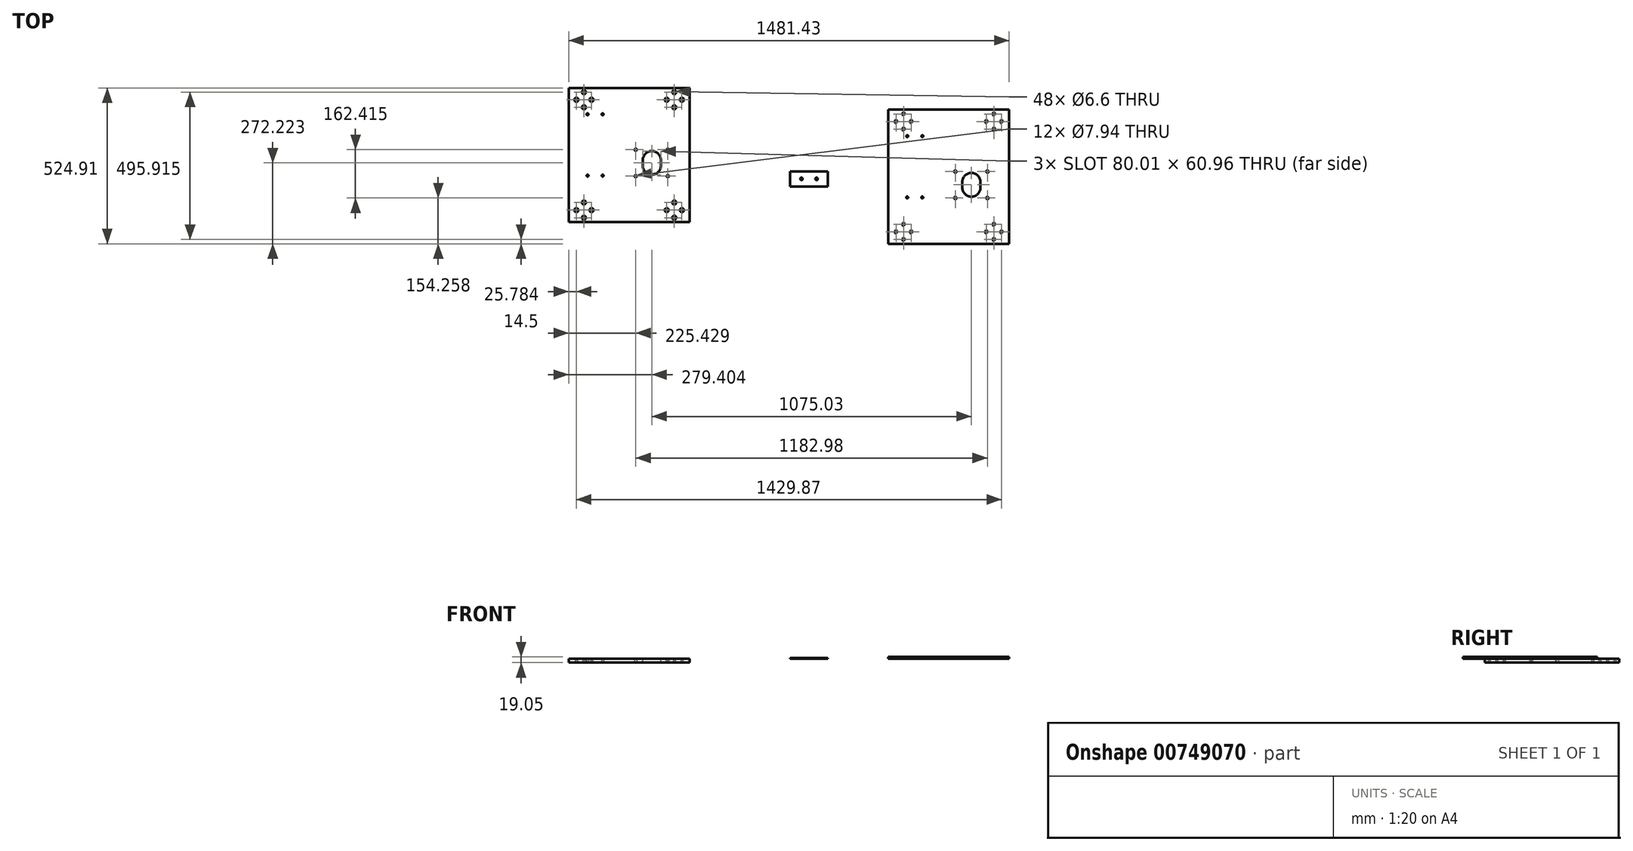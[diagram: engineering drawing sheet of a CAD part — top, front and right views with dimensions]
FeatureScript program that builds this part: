
annotation { "Feature Type Name" : "Feature", "Feature Type Description" : "" }
export const myFeature = defineFeature(function(context is Context, id is Id, definition is map)
    precondition{}
    {
        {
            var Q0;
            Q0=qCreatedBy(makeId("Top.planeOp"),FACE);
            var sketch = newSketch(context, id + "F0", { "sketchPlane" : qUnion([Q0])});
            skLineSegment(sketch, "E0.bottom", {"start": v(0, 0) * mm, "end": v(406.4, 0) * mm});
            skLineSegment(sketch, "E0.top", {"start": v(0, 451.4) * mm, "end": v(406.4, 451.4) * mm});
            skLineSegment(sketch, "E0.left", {"start": v(0, 0) * mm, "end": v(0, 451.4) * mm});
            skLineSegment(sketch, "E0.right", {"start": v(406.4, 0) * mm, "end": v(406.4, 451.4) * mm});
            skLineSegment(sketch, "E1", {"start": v(406.4, 40) * mm, "end": v(0, 40) * mm, "construction": true});
            skLineSegment(sketch, "E2", {"start": v(0, 80) * mm, "end": v(406.4, 80) * mm, "construction": true});
            skLineSegment(sketch, "E3", {"start": v(0, 225.7) * mm, "end": v(406.4, 225.7) * mm, "construction": true});
            skLineSegment(sketch, "E4", {"start": v(253.84, 0) * mm, "end": v(253.84, 225.7) * mm, "construction": true});
            skLineSegment(sketch, "E5", {"start": v(152.56, 0) * mm, "end": v(152.56, 225.7) * mm, "construction": true});
            skLineSegment(sketch, "E6", {"start": v(51.28, 0) * mm, "end": v(51.28, 225.7) * mm, "construction": true});
            skLineSegment(sketch, "E7", {"start": v(355.12, 0) * mm, "end": v(355.12, 225.7) * mm, "construction": true});
            skPoint(sketch, "E8", {"position": v(25.78, 40) * mm});
            skPoint(sketch, "E9", {"position": v(51.28, 14.5) * mm});
            skPoint(sketch, "E10", {"position": v(355.12, 14.5) * mm});
            skPoint(sketch, "E11", {"position": v(329.62, 40) * mm});
            skPoint(sketch, "E12.MirrorP", {"position": v(76.78, 40) * mm});
            skPoint(sketch, "E13.MirrorP", {"position": v(51.28, 65.5) * mm});
            skPoint(sketch, "E14.MirrorP", {"position": v(380.62, 40) * mm});
            skPoint(sketch, "E15.MirrorP", {"position": v(355.12, 65.5) * mm});
            skPoint(sketch, "E16.MirrorP", {"position": v(76.78, 411.4) * mm});
            skPoint(sketch, "E17.MirrorP", {"position": v(25.78, 411.4) * mm});
            skPoint(sketch, "E18.MirrorP", {"position": v(51.28, 385.9) * mm});
            skPoint(sketch, "E19.MirrorP", {"position": v(51.28, 436.9) * mm});
            skPoint(sketch, "E20.MirrorP", {"position": v(329.62, 411.4) * mm});
            skPoint(sketch, "E21.MirrorP", {"position": v(355.12, 436.9) * mm});
            skPoint(sketch, "E22.MirrorP", {"position": v(355.12, 385.9) * mm});
            skPoint(sketch, "E23.MirrorP", {"position": v(380.62, 411.4) * mm});
            skLineSegment(sketch, "E24", {"start": v(406.4, 22.5) * mm, "end": v(0, 22.5) * mm, "construction": true});
            skLineSegment(sketch, "E25.MirrorCS", {"start": v(406.4, 428.9) * mm, "end": v(0, 428.9) * mm, "construction": true});
            skLineSegment(sketch, "E26", {"start": v(406.4, 411.4) * mm, "end": v(0, 411.4) * mm, "construction": true});
            skSolve(sketch);
        }
        {
            var Q0;
            Q0 = qSketchRegion(id + "F0", true);
            extrude(context, id + "F1", {"entities" : qUnion([Q0]), "depth" : 6.35 * mm, "offsetDistance" : 25 * mm});
        }
        {
            var Q0;
            Q0=sQuery(id+"F0.wireOp",VERTEX,"E22.MirrorP");
            var Q1;
            Q1=sQuery(id+"F0.wireOp",VERTEX,"E20.MirrorP");
            var Q2;
            Q2=sQuery(id+"F0.wireOp",VERTEX,"E21.MirrorP");
            var Q3;
            Q3=sQuery(id+"F0.wireOp",VERTEX,"E23.MirrorP");
            var Q4;
            Q4=sQuery(id+"F0.wireOp",VERTEX,"6af4f434-9a47-4052-8a1d-334fbff560f00.MirrorP");
            var Q5;
            Q5=sQuery(id+"F0.wireOp",VERTEX,"22235c4d-a030-4c03-83f7-dc97571283850.MirrorP");
            var Q6;
            Q6=sQuery(id+"F0.wireOp",VERTEX,"707f3ab1-3b27-4a9b-9bac-d71ad12bc8670.MirrorP");
            var Q7;
            Q7=sQuery(id+"F0.wireOp",VERTEX,"0a2d6588-346a-4415-8c80-8cd4bdffcf730.MirrorP");
            var Q8;
            Q8=sQuery(id+"F0.wireOp",VERTEX,"356fdae6-4249-49e8-b5b6-363c88dfb11d0.MirrorP");
            var Q9;
            Q9=sQuery(id+"F0.wireOp",VERTEX,"ac791697-a596-4bc9-b602-2fd92d7f03d00.MirrorP");
            var Q10;
            Q10=sQuery(id+"F0.wireOp",VERTEX,"2612b1d6-8924-45c9-9463-7b17644163d90.MirrorP");
            var Q11;
            Q11=sQuery(id+"F0.wireOp",VERTEX,"3fab72b2-7065-4257-901b-2c846910f1860.MirrorP");
            var Q12;
            Q12=sQuery(id+"F0.wireOp",VERTEX,"E16.MirrorP");
            var Q13;
            Q13=sQuery(id+"F0.wireOp",VERTEX,"E18.MirrorP");
            var Q14;
            Q14=sQuery(id+"F0.wireOp",VERTEX,"E17.MirrorP");
            var Q15;
            Q15=sQuery(id+"F0.wireOp",VERTEX,"E19.MirrorP");
            var Q16;
            Q16=sQuery(id+"F0.wireOp",VERTEX,"E13.MirrorP");
            var Q17;
            Q17=sQuery(id+"F0.wireOp",VERTEX,"E8");
            var Q18;
            Q18=sQuery(id+"F0.wireOp",VERTEX,"E9");
            var Q19;
            Q19=sQuery(id+"F0.wireOp",VERTEX,"E12.MirrorP");
            var Q20;
            Q20=sQuery(id+"F0.wireOp",VERTEX,"a2639b54-34fe-431f-abc9-276ef6bb1585");
            var Q21;
            Q21=sQuery(id+"F0.wireOp",VERTEX,"f26440d5-e4e3-4b70-a236-2be0b37ad0070.MirrorP");
            var Q22;
            Q22=sQuery(id+"F0.wireOp",VERTEX,"72e066eb-c41a-45e6-b766-06aafbe1a7a1");
            var Q23;
            Q23=sQuery(id+"F0.wireOp",VERTEX,"cab5caa1-8496-43b3-b20d-0bef22b276cc0.MirrorP");
            var Q24;
            Q24=sQuery(id+"F0.wireOp",VERTEX,"af764541-ac38-46f8-b840-c88313bd4171");
            var Q25;
            Q25=sQuery(id+"F0.wireOp",VERTEX,"6547167e-a008-43e8-a996-357f91e35cae0.MirrorP");
            var Q26;
            Q26=sQuery(id+"F0.wireOp",VERTEX,"47519a64-4156-4ac7-a9d7-64227d0fa828");
            var Q27;
            Q27=sQuery(id+"F0.wireOp",VERTEX,"6742967f-264e-4da4-b44c-0f49fa165dfd0.MirrorP");
            var Q28;
            Q28=sQuery(id+"F0.wireOp",VERTEX,"E11");
            var Q29;
            Q29=sQuery(id+"F0.wireOp",VERTEX,"E15.MirrorP");
            var Q30;
            Q30=sQuery(id+"F0.wireOp",VERTEX,"E14.MirrorP");
            var Q31;
            Q31=sQuery(id+"F0.wireOp",VERTEX,"E10");
            var Q32;
            Q32=makeQuery(id+"F1.opExtrude","SWEPT_BODY",BODY,{"disambiguationData":[OSD([sQuery(id+"F0.wireOp",EDGE,"E0.bottom"),sQuery(id+"F0.wireOp",EDGE,"E0.top"),sQuery(id+"F0.wireOp",EDGE,"E0.left"),sQuery(id+"F0.wireOp",EDGE,"E0.right")])]});
            hole(context, id + "F2", {"style" : HoleStyle.C_SINK, "endStyle" : HoleEndStyle.BLIND, "oppositeDirection" : true, "standardTappedOrClearance" : lookupTablePath({ "standard" : "ISO", "fit" : "Normal", "size" : "M6", "type" : "Clearance" }), "standardBlindInLast" : lookupTablePath({ "fit" : "Standard", "standard" : "ISO", "size" : "M6", "type" : "Clearance" }), "holeDiameter" : 6.6 * mm, "cSinkDiameter" : 13.44 * mm, "cSinkAngle" : 90 * degree, "majorDiameter" : 5 * mm, "holeDepth" : 12 * mm, "isTappedThrough" : true, "tappedDepth" : 1.9 * mm, "tapClearance" : 3, "locations" : qUnion([Q0, Q1, Q2, Q3, Q4, Q5, Q6, Q7, Q8, Q9, Q10, Q11, Q12, Q13, Q14, Q15, Q16, Q17, Q18, Q19, Q20, Q21, Q22, Q23, Q24, Q25, Q26, Q27, Q28, Q29, Q30, Q31]), "scope" : qUnion([Q32])});
        }
        {
            var Q0;
            Q0=makeQuery(id+"F0.imprint","IMPRINT",FACE,{"disambiguationData":[TD([[makeQuery(id+"F0.imprint","IMPRINT",EDGE,{"derivedFrom":sQuery(id+"F0.wireOp",EDGE,"E0.bottom")}),1.0]])]});
            var sketch = newSketch(context, id + "F3", { "sketchPlane" : qUnion([Q0])});
            skLineSegment(sketch, "E27", {"start": v(0, 362.5) * mm, "end": v(406.4, 362.5) * mm, "construction": true});
            skLineSegment(sketch, "E28", {"start": v(203.2, 362.5) * mm, "end": v(203.2, 0) * mm, "construction": true});
            skLineSegment(sketch, "E29", {"start": v(0, 451.44) * mm, "end": v(0, 0) * mm, "construction": true});
            skLineSegment(sketch, "E30", {"start": v(0, 206.65) * mm, "end": v(448.74, 206.65) * mm, "construction": true});
            skLineSegment(sketch, "E31.bottom", {"start": v(342.9, 143.15) * mm, "end": v(215.9, 143.15) * mm, "construction": true});
            skLineSegment(sketch, "E31.top", {"start": v(342.9, 270.15) * mm, "end": v(215.9, 270.15) * mm, "construction": true});
            skLineSegment(sketch, "E31.left", {"start": v(342.9, 143.15) * mm, "end": v(342.9, 270.15) * mm, "construction": true});
            skLineSegment(sketch, "E31.right", {"start": v(215.9, 143.15) * mm, "end": v(215.9, 270.15) * mm, "construction": true});
            skPoint(sketch, "E31.middle", {"position": v(279.4, 206.65) * mm});
            skLineSegment(sketch, "E32", {"start": v(0, 156.12) * mm, "end": v(408.9, 156.12) * mm, "construction": true});
            skPoint(sketch, "E33", {"position": v(114.3, 156.12) * mm});
            skLineSegment(sketch, "E34.0", {"start": v(0, 451.4) * mm, "end": v(406.4, 451.4) * mm, "construction": true});
            skPoint(sketch, "E35", {"position": v(333.38, 243.16) * mm});
            skLineSegment(sketch, "E36", {"start": v(279.4, 156.12) * mm, "end": v(279.4, 270.15) * mm, "construction": true});
            skPoint(sketch, "E37.MirrorP", {"position": v(225.43, 243.16) * mm});
            skPoint(sketch, "E38", {"position": v(333.38, 154.26) * mm});
            skPoint(sketch, "E39.MirrorP", {"position": v(225.43, 154.26) * mm});
            skArc(sketch, "E40", {"start": v(248.92, 189.18) * mm, "mid": v(279.4, 158.7) * mm, "end": v(309.88, 189.18) * mm});
            skArc(sketch, "E41", {"start": v(309.84, 206.65) * mm, "mid": v(279.4, 238.71) * mm, "end": v(248.96, 206.65) * mm});
            skLineSegment(sketch, "E42", {"start": v(309.88, 189.18) * mm, "end": v(309.88, 208.23) * mm});
            skLineSegment(sketch, "E43", {"start": v(248.92, 189.18) * mm, "end": v(248.92, 208.23) * mm});
            skArc(sketch, "E44.trimOffspring", {"start": v(309.88, 208.23) * mm, "mid": v(279.4, 238.71) * mm, "end": v(248.92, 208.23) * mm});
            skLineSegment(sketch, "E45", {"start": v(88.9, 451.4) * mm, "end": v(88.9, 88.98) * mm, "construction": true});
            skPoint(sketch, "E46", {"position": v(63.5, 362.5) * mm});
            skPoint(sketch, "E47.MirrorP", {"position": v(114.3, 362.5) * mm});
            skPoint(sketch, "E48.MirrorP", {"position": v(63.5, 156.12) * mm});
            skSolve(sketch);
        }
        {
            var Q0;
            Q0 = qSketchRegion(id + "F3", true);
            extrude(context, id + "F4", {"entities" : qUnion([Q0]), "operationType" : NewBodyOperationType.REMOVE, "depth" : 25.4 * mm, "offsetDistance" : 25.4 * mm});
        }
        {
            var Q0;
            Q0=sQuery(id+"F3.wireOp",VERTEX,"E46");
            var Q1;
            Q1=sQuery(id+"F3.wireOp",VERTEX,"E47.MirrorP");
            var Q2;
            Q2=sQuery(id+"F3.wireOp",VERTEX,"E48.MirrorP");
            var Q3;
            Q3=sQuery(id+"F3.wireOp",VERTEX,"E33");
            var Q4;
            Q4=makeQuery(id+"F1.opExtrude","SWEPT_BODY",BODY,{"disambiguationData":[OSD([sQuery(id+"F0.wireOp",EDGE,"E0.bottom"),sQuery(id+"F0.wireOp",EDGE,"E0.top"),sQuery(id+"F0.wireOp",EDGE,"E0.left"),sQuery(id+"F0.wireOp",EDGE,"E0.right")])]});
            hole(context, id + "F5", {"style" : HoleStyle.SIMPLE, "endStyle" : HoleEndStyle.BLIND, "oppositeDirection" : true, "standardTappedOrClearance" : lookupTablePath({ "standard" : "ANSI", "engagement" : "75%", "pitch" : "18 tpi", "size" : "5/16", "type" : "Tapped" }), "standardBlindInLast" : lookupTablePath({ "standard" : "ANSI", "engagement" : "75%", "pitch" : "18 tpi", "size" : "5/16", "type" : "Tapped" }), "holeDiameter" : 6.53 * mm, "majorDiameter" : 7.94 * mm, "showTappedDepth" : true, "holeDepth" : 20.1 * mm, "isTappedThrough" : true, "tappedDepth" : 15.88 * mm, "tapClearance" : 3, "locations" : qUnion([Q0, Q1, Q2, Q3]), "scope" : qUnion([Q4])});
        }
        {
            var Q0;
            Q0=qCreatedBy(makeId("Top.planeOp"),FACE);
            var sketch = newSketch(context, id + "F6", { "sketchPlane" : qUnion([Q0])});
            skLineSegment(sketch, "E49.bottom", {"start": v(-1075.03, 73.51) * mm, "end": v(-668.63, 73.51) * mm});
            skLineSegment(sketch, "E49.top", {"start": v(-1075.03, 524.91) * mm, "end": v(-668.63, 524.91) * mm});
            skLineSegment(sketch, "E49.left", {"start": v(-1075.03, 73.51) * mm, "end": v(-1075.03, 524.91) * mm});
            skLineSegment(sketch, "E49.right", {"start": v(-668.63, 73.51) * mm, "end": v(-668.63, 524.91) * mm});
            skLineSegment(sketch, "E50", {"start": v(-668.63, 113.51) * mm, "end": v(-1075.03, 113.51) * mm, "construction": true});
            skLineSegment(sketch, "E51", {"start": v(-1075.03, 153.51) * mm, "end": v(-668.63, 153.51) * mm, "construction": true});
            skLineSegment(sketch, "E52", {"start": v(-1075.03, 299.21) * mm, "end": v(-668.63, 299.21) * mm, "construction": true});
            skLineSegment(sketch, "E53", {"start": v(-821.19, 73.51) * mm, "end": v(-821.19, 299.21) * mm, "construction": true});
            skLineSegment(sketch, "E54", {"start": v(-922.47, 73.51) * mm, "end": v(-922.47, 299.21) * mm, "construction": true});
            skLineSegment(sketch, "E55", {"start": v(-1023.75, 73.51) * mm, "end": v(-1023.75, 299.21) * mm, "construction": true});
            skLineSegment(sketch, "E56", {"start": v(-719.9, 73.51) * mm, "end": v(-719.9, 299.21) * mm, "construction": true});
            skPoint(sketch, "E57", {"position": v(-1049.25, 113.51) * mm});
            skPoint(sketch, "E58", {"position": v(-1023.75, 88.01) * mm});
            skPoint(sketch, "E59", {"position": v(-719.9, 88.01) * mm});
            skPoint(sketch, "E60", {"position": v(-745.4, 113.51) * mm});
            skPoint(sketch, "E61.MirrorP", {"position": v(-998.25, 113.51) * mm});
            skPoint(sketch, "E62.MirrorP", {"position": v(-1023.75, 139.01) * mm});
            skPoint(sketch, "E63.MirrorP", {"position": v(-694.4, 113.51) * mm});
            skPoint(sketch, "E64.MirrorP", {"position": v(-719.9, 139.01) * mm});
            skPoint(sketch, "E65.MirrorP", {"position": v(-998.25, 484.91) * mm});
            skPoint(sketch, "E66.MirrorP", {"position": v(-1049.25, 484.91) * mm});
            skPoint(sketch, "E67.MirrorP", {"position": v(-1023.75, 459.41) * mm});
            skPoint(sketch, "E68.MirrorP", {"position": v(-1023.75, 510.41) * mm});
            skPoint(sketch, "E69.MirrorP", {"position": v(-745.4, 484.91) * mm});
            skPoint(sketch, "E70.MirrorP", {"position": v(-719.9, 510.41) * mm});
            skPoint(sketch, "E71.MirrorP", {"position": v(-719.9, 459.41) * mm});
            skPoint(sketch, "E72.MirrorP", {"position": v(-694.4, 484.91) * mm});
            skLineSegment(sketch, "E73", {"start": v(-668.63, 96.01) * mm, "end": v(-1075.03, 96.01) * mm, "construction": true});
            skLineSegment(sketch, "E74.MirrorCS", {"start": v(-668.63, 502.41) * mm, "end": v(-1075.03, 502.41) * mm, "construction": true});
            skLineSegment(sketch, "E75", {"start": v(-668.63, 484.91) * mm, "end": v(-1075.03, 484.91) * mm, "construction": true});
            skLineSegment(sketch, "E76", {"start": v(-1075.03, 436.01) * mm, "end": v(-668.63, 436.01) * mm, "construction": true});
            skLineSegment(sketch, "E77", {"start": v(-871.83, 436.01) * mm, "end": v(-871.83, 73.51) * mm, "construction": true});
            skLineSegment(sketch, "E78", {"start": v(-1075.03, 524.95) * mm, "end": v(-1075.03, 73.51) * mm, "construction": true});
            skLineSegment(sketch, "E79", {"start": v(-1075.03, 280.16) * mm, "end": v(-626.29, 280.16) * mm, "construction": true});
            skLineSegment(sketch, "E80.bottom", {"start": v(-732.13, 216.66) * mm, "end": v(-859.13, 216.66) * mm, "construction": true});
            skLineSegment(sketch, "E80.top", {"start": v(-732.13, 343.66) * mm, "end": v(-859.13, 343.66) * mm, "construction": true});
            skLineSegment(sketch, "E80.left", {"start": v(-732.13, 216.66) * mm, "end": v(-732.13, 343.66) * mm, "construction": true});
            skLineSegment(sketch, "E80.right", {"start": v(-859.13, 216.66) * mm, "end": v(-859.13, 343.66) * mm, "construction": true});
            skPoint(sketch, "E80.middle", {"position": v(-795.63, 280.16) * mm});
            skLineSegment(sketch, "E81", {"start": v(-1075.03, 229.64) * mm, "end": v(-666.12, 229.64) * mm, "construction": true});
            skPoint(sketch, "E82", {"position": v(-960.73, 229.64) * mm});
            skLineSegment(sketch, "E83.0", {"start": v(-1075.03, 524.91) * mm, "end": v(-668.63, 524.91) * mm, "construction": true});
            skPoint(sketch, "E84", {"position": v(-741.65, 316.67) * mm});
            skLineSegment(sketch, "E85", {"start": v(-795.63, 229.64) * mm, "end": v(-795.63, 343.66) * mm, "construction": true});
            skPoint(sketch, "E86.MirrorP", {"position": v(-849.6, 316.67) * mm});
            skPoint(sketch, "E87", {"position": v(-741.65, 227.77) * mm});
            skPoint(sketch, "E88.MirrorP", {"position": v(-849.6, 227.77) * mm});
            skArc(sketch, "E89", {"start": v(-826.1, 262.7) * mm, "mid": v(-795.63, 232.22) * mm, "end": v(-765.15, 262.7) * mm});
            skArc(sketch, "E90", {"start": v(-765.19, 280.16) * mm, "mid": v(-795.63, 312.23) * mm, "end": v(-826.06, 280.16) * mm});
            skLineSegment(sketch, "E91", {"start": v(-765.15, 262.7) * mm, "end": v(-765.15, 281.75) * mm});
            skLineSegment(sketch, "E92", {"start": v(-826.1, 262.7) * mm, "end": v(-826.1, 281.75) * mm});
            skArc(sketch, "E93.trimOffspring", {"start": v(-765.15, 281.75) * mm, "mid": v(-795.63, 312.23) * mm, "end": v(-826.1, 281.75) * mm});
            skLineSegment(sketch, "E94", {"start": v(-986.13, 524.91) * mm, "end": v(-986.13, 162.5) * mm, "construction": true});
            skPoint(sketch, "E95", {"position": v(-1011.53, 436.01) * mm});
            skPoint(sketch, "E96.MirrorP", {"position": v(-960.73, 436.01) * mm});
            skPoint(sketch, "E97.MirrorP", {"position": v(-1011.53, 229.64) * mm});
            skSolve(sketch);
        }
        {
            var Q0;
            Q0 = qSketchRegion(id + "F6", true);
            extrude(context, id + "F7", {"entities" : qUnion([Q0]), "oppositeDirection" : true, "depth" : 12.7 * mm, "offsetDistance" : 25.4 * mm});
        }
        {
            var Q0;
            Q0=sQuery(id+"F6.wireOp",VERTEX,"E58");
            var Q1;
            Q1=sQuery(id+"F6.wireOp",VERTEX,"E57");
            var Q2;
            Q2=sQuery(id+"F6.wireOp",VERTEX,"E61.MirrorP");
            var Q3;
            Q3=sQuery(id+"F6.wireOp",VERTEX,"E62.MirrorP");
            var Q4;
            Q4=sQuery(id+"F6.wireOp",VERTEX,"E67.MirrorP");
            var Q5;
            Q5=sQuery(id+"F6.wireOp",VERTEX,"E66.MirrorP");
            var Q6;
            Q6=sQuery(id+"F6.wireOp",VERTEX,"E68.MirrorP");
            var Q7;
            Q7=sQuery(id+"F6.wireOp",VERTEX,"E65.MirrorP");
            var Q8;
            Q8=sQuery(id+"F6.wireOp",VERTEX,"E71.MirrorP");
            var Q9;
            Q9=sQuery(id+"F6.wireOp",VERTEX,"E69.MirrorP");
            var Q10;
            Q10=sQuery(id+"F6.wireOp",VERTEX,"E72.MirrorP");
            var Q11;
            Q11=sQuery(id+"F6.wireOp",VERTEX,"E70.MirrorP");
            var Q12;
            Q12=sQuery(id+"F6.wireOp",VERTEX,"E64.MirrorP");
            var Q13;
            Q13=sQuery(id+"F6.wireOp",VERTEX,"E59");
            var Q14;
            Q14=sQuery(id+"F6.wireOp",VERTEX,"E63.MirrorP");
            var Q15;
            Q15=sQuery(id+"F6.wireOp",VERTEX,"E60");
            var Q16;
            Q16=makeQuery(id+"F7.opExtrude","SWEPT_BODY",BODY,{"disambiguationData":[OSD([sQuery(id+"F6.wireOp",EDGE,"E49.bottom"),sQuery(id+"F6.wireOp",EDGE,"E49.top"),sQuery(id+"F6.wireOp",EDGE,"E49.left"),sQuery(id+"F6.wireOp",EDGE,"E49.right"),sQuery(id+"F6.wireOp",EDGE,"E91"),sQuery(id+"F6.wireOp",EDGE,"E92"),sQuery(id+"F6.wireOp",EDGE,"E90"),sQuery(id+"F6.wireOp",EDGE,"E89")])]});
            hole(context, id + "F8", {"style" : HoleStyle.C_SINK, "endStyle" : HoleEndStyle.BLIND, "standardTappedOrClearance" : lookupTablePath({ "standard" : "ISO", "fit" : "Normal", "size" : "M6", "type" : "Clearance" }), "standardBlindInLast" : lookupTablePath({ "fit" : "Standard", "standard" : "ISO", "size" : "M6", "type" : "Clearance" }), "holeDiameter" : 6.6 * mm, "cSinkDiameter" : 13.44 * mm, "cSinkAngle" : 90 * degree, "majorDiameter" : 6.35 * mm, "holeDepth" : 18.87 * mm, "isTappedThrough" : true, "tappedDepth" : 15.88 * mm, "tapClearance" : 3, "locations" : qUnion([Q0, Q1, Q2, Q3, Q4, Q5, Q6, Q7, Q8, Q9, Q10, Q11, Q12, Q13, Q14, Q15]), "scope" : qUnion([Q16])});
        }
        {
            var Q0;
            Q0=sQuery(id+"F6.wireOp",VERTEX,"E82");
            var Q1;
            Q1=sQuery(id+"F6.wireOp",VERTEX,"E97.MirrorP");
            var Q2;
            Q2=sQuery(id+"F6.wireOp",VERTEX,"E96.MirrorP");
            var Q3;
            Q3=sQuery(id+"F6.wireOp",VERTEX,"E95");
            var Q4;
            Q4=makeQuery(id+"F7.opExtrude","SWEPT_BODY",BODY,{"disambiguationData":[OSD([sQuery(id+"F6.wireOp",EDGE,"E49.bottom"),sQuery(id+"F6.wireOp",EDGE,"E49.top"),sQuery(id+"F6.wireOp",EDGE,"E49.left"),sQuery(id+"F6.wireOp",EDGE,"E49.right"),sQuery(id+"F6.wireOp",EDGE,"E91"),sQuery(id+"F6.wireOp",EDGE,"E92"),sQuery(id+"F6.wireOp",EDGE,"E90"),sQuery(id+"F6.wireOp",EDGE,"E89")])]});
            hole(context, id + "F9", {"style" : HoleStyle.SIMPLE, "endStyle" : HoleEndStyle.BLIND, "standardTappedOrClearance" : lookupTablePath({ "standard" : "ANSI", "engagement" : "75%", "pitch" : "18 tpi", "size" : "5/16", "type" : "Tapped" }), "standardBlindInLast" : lookupTablePath({ "standard" : "ANSI", "engagement" : "75%", "pitch" : "18 tpi", "size" : "5/16", "type" : "Tapped" }), "holeDiameter" : 6.53 * mm, "majorDiameter" : 7.94 * mm, "showTappedDepth" : true, "holeDepth" : 20.1 * mm, "isTappedThrough" : true, "tappedDepth" : 15.88 * mm, "tapClearance" : 3, "locations" : qUnion([Q0, Q1, Q2, Q3]), "scope" : qUnion([Q4])});
        }
        {
            var Q0;
            Q0=sQuery(id+"F6.wireOp",VERTEX,"E87");
            var Q1;
            Q1=sQuery(id+"F6.wireOp",VERTEX,"E88.MirrorP");
            var Q2;
            Q2=sQuery(id+"F6.wireOp",VERTEX,"E86.MirrorP");
            var Q3;
            Q3=sQuery(id+"F6.wireOp",VERTEX,"E84");
            var Q4;
            Q4=makeQuery(id+"F7.opExtrude","SWEPT_BODY",BODY,{"disambiguationData":[OSD([sQuery(id+"F6.wireOp",EDGE,"E49.bottom"),sQuery(id+"F6.wireOp",EDGE,"E49.top"),sQuery(id+"F6.wireOp",EDGE,"E49.left"),sQuery(id+"F6.wireOp",EDGE,"E49.right"),sQuery(id+"F6.wireOp",EDGE,"E91"),sQuery(id+"F6.wireOp",EDGE,"E92"),sQuery(id+"F6.wireOp",EDGE,"E90"),sQuery(id+"F6.wireOp",EDGE,"E89")])]});
            hole(context, id + "F10", {"style" : HoleStyle.SIMPLE, "endStyle" : HoleEndStyle.BLIND, "standardTappedOrClearance" : lookupTablePath({ "standard" : "ANSI", "engagement" : "75%", "pitch" : "16 tpi", "size" : "3/8", "type" : "Tapped" }), "standardBlindInLast" : lookupTablePath({ "standard" : "ANSI", "engagement" : "75%", "pitch" : "16 tpi", "size" : "3/8", "type" : "Tapped" }), "holeDiameter" : 7.94 * mm, "majorDiameter" : 9.52 * mm, "showTappedDepth" : true, "holeDepth" : 20.65 * mm, "isTappedThrough" : true, "tappedDepth" : 15.88 * mm, "tapClearance" : 3, "locations" : qUnion([Q0, Q1, Q2, Q3]), "scope" : qUnion([Q4])});
        }
        {
            var Q0;
            Q0=sQuery(id+"F3.wireOp",VERTEX,"E38");
            var Q1;
            Q1=sQuery(id+"F3.wireOp",VERTEX,"E35");
            var Q2;
            Q2=sQuery(id+"F3.wireOp",VERTEX,"E37.MirrorP");
            var Q3;
            Q3=sQuery(id+"F3.wireOp",VERTEX,"E39.MirrorP");
            var Q4;
            Q4=makeQuery(id+"F1.opExtrude","SWEPT_BODY",BODY,{"disambiguationData":[OSD([sQuery(id+"F0.wireOp",EDGE,"E0.bottom"),sQuery(id+"F0.wireOp",EDGE,"E0.top"),sQuery(id+"F0.wireOp",EDGE,"E0.left"),sQuery(id+"F0.wireOp",EDGE,"E0.right")])]});
            hole(context, id + "F11", {"style" : HoleStyle.SIMPLE, "endStyle" : HoleEndStyle.BLIND, "oppositeDirection" : true, "standardTappedOrClearance" : lookupTablePath({ "standard" : "ANSI", "engagement" : "75%", "pitch" : "16 tpi", "size" : "3/8", "type" : "Tapped" }), "standardBlindInLast" : lookupTablePath({ "standard" : "ANSI", "engagement" : "75%", "pitch" : "16 tpi", "size" : "3/8", "type" : "Tapped" }), "holeDiameter" : 7.94 * mm, "majorDiameter" : 9.52 * mm, "showTappedDepth" : true, "holeDepth" : 20.65 * mm, "isTappedThrough" : true, "tappedDepth" : 15.88 * mm, "tapClearance" : 3, "locations" : qUnion([Q0, Q1, Q2, Q3]), "scope" : qUnion([Q4])});
        }
        {
            var Q0;
            Q0=qCreatedBy(makeId("Top.planeOp"),FACE);
            var sketch = newSketch(context, id + "F12", { "sketchPlane" : qUnion([Q0])});
            skLineSegment(sketch, "E98.bottom", {"start": v(-203.2, 193.27) * mm, "end": v(-330.2, 193.27) * mm});
            skLineSegment(sketch, "E98.top", {"start": v(-203.2, 244.07) * mm, "end": v(-330.2, 244.07) * mm});
            skLineSegment(sketch, "E98.left", {"start": v(-203.2, 193.27) * mm, "end": v(-203.2, 244.07) * mm});
            skLineSegment(sketch, "E98.right", {"start": v(-330.2, 193.27) * mm, "end": v(-330.2, 244.07) * mm});
            skLineSegment(sketch, "E99", {"start": v(-203.2, 218.67) * mm, "end": v(-330.2, 218.67) * mm, "construction": true});
            skLineSegment(sketch, "E100", {"start": v(-266.7, 244.07) * mm, "end": v(-266.7, 193.27) * mm, "construction": true});
            skPoint(sketch, "E101", {"position": v(-241.3, 218.67) * mm});
            skPoint(sketch, "E102.MirrorP", {"position": v(-292.1, 218.67) * mm});
            skSolve(sketch);
        }
        {
            var Q0;
            Q0 = qSketchRegion(id + "F12", true);
            extrude(context, id + "F13", {"entities" : qUnion([Q0]), "depth" : 3.17 * mm, "offsetDistance" : 25.4 * mm});
        }
        {
            var Q0;
            Q0=sQuery(id+"F12.wireOp",VERTEX,"E101");
            var Q1;
            Q1=sQuery(id+"F12.wireOp",VERTEX,"E102.MirrorP");
            var Q2;
            Q2=makeQuery(id+"F13.opExtrude","SWEPT_BODY",BODY,{"disambiguationData":[OSD([sQuery(id+"F12.wireOp",EDGE,"E98.bottom"),sQuery(id+"F12.wireOp",EDGE,"E98.top"),sQuery(id+"F12.wireOp",EDGE,"E98.left"),sQuery(id+"F12.wireOp",EDGE,"E98.right")])]});
            hole(context, id + "F14", {"style" : HoleStyle.SIMPLE, "endStyle" : HoleEndStyle.BLIND, "oppositeDirection" : true, "standardTappedOrClearance" : lookupTablePath({ "standard" : "ANSI", "fit" : "Normal (ASME)", "size" : "5/16", "type" : "Clearance" }), "standardBlindInLast" : lookupTablePath({ "fit" : "Free", "standard" : "ANSI", "size" : "5/16", "type" : "Clearance" }), "holeDiameter" : 8.43 * mm, "majorDiameter" : 9.52 * mm, "holeDepth" : 20.65 * mm, "isTappedThrough" : true, "tappedDepth" : 15.9 * mm, "tapClearance" : 3, "locations" : qUnion([Q0, Q1]), "scope" : qUnion([Q2])});
        }
        {
            var Q0;
            Q0=makeQuery(id+"F1.opExtrude","SWEPT_BODY",BODY,{"disambiguationData":[OSD([sQuery(id+"F0.wireOp",EDGE,"E0.bottom"),sQuery(id+"F0.wireOp",EDGE,"E0.top"),sQuery(id+"F0.wireOp",EDGE,"E0.left"),sQuery(id+"F0.wireOp",EDGE,"E0.right")])]});
            transform(context, id + "F15", {"entities" : qUnion([Q0]), "transformType" : TransformType.TRANSLATION_3D, "dx" : 0 * mm, "dy" : 0 * mm, "dz" : 0 * mm, "makeCopy" : true});
        }
    });
